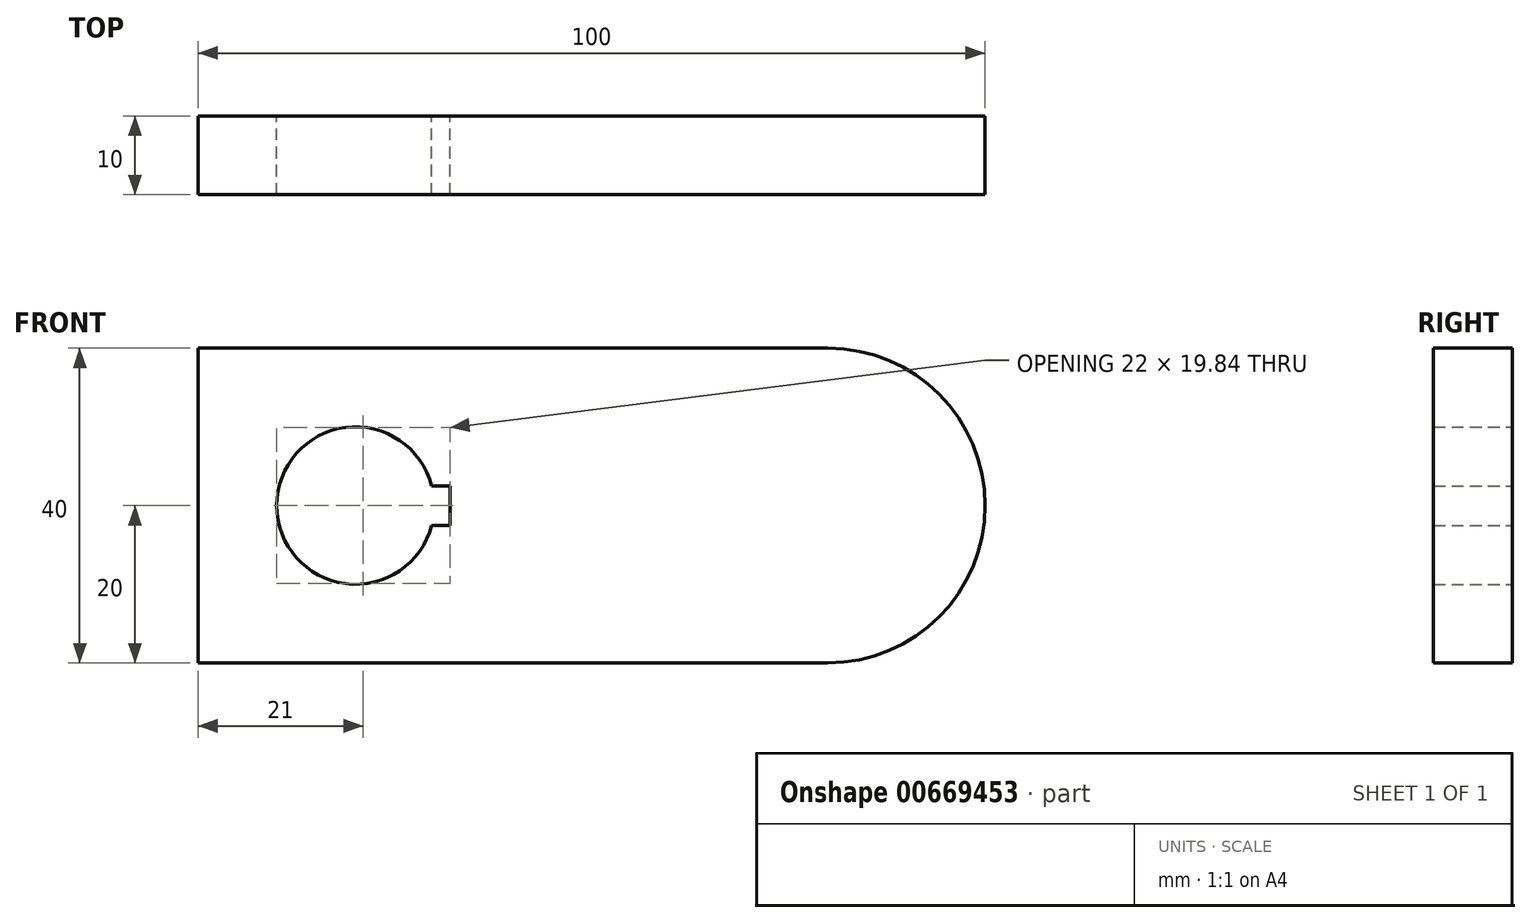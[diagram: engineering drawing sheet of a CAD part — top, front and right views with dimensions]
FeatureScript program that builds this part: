
annotation { "Feature Type Name" : "Feature", "Feature Type Description" : "" }
export const myFeature = defineFeature(function(context is Context, id is Id, definition is map)
    precondition{}
    {
        {
            var Q0;
            Q0=qCreatedBy(makeId("Front.planeOp"),FACE);
            var sketch = newSketch(context, id + "F0", { "sketchPlane" : qUnion([Q0])});
            skLineSegment(sketch, "E0.bottom", {"start": v(-80, 40) * mm, "end": v(0, 40) * mm});
            skLineSegment(sketch, "E0.top", {"start": v(-80, 0) * mm, "end": v(0, 0) * mm});
            skLineSegment(sketch, "E0.left", {"start": v(-80, 40) * mm, "end": v(-80, 0) * mm});
            skArc(sketch, "E1", {"start": v(-50.32, 22.5) * mm, "mid": v(-70, 20) * mm, "end": v(-50.32, 17.5) * mm});
            skPoint(sketch, "E2.centerSnap0", {"position": v(0, 20) * mm});
            skArc(sketch, "E3", {"start": v(0, 0) * mm, "mid": v(20, 20) * mm, "end": v(0, 40) * mm});
            skLineSegment(sketch, "E4", {"start": v(-60, 20) * mm, "end": v(-48, 20) * mm, "construction": true});
            skLineSegment(sketch, "E5", {"start": v(-48, 20) * mm, "end": v(-48, 22.5) * mm});
            skLineSegment(sketch, "E6", {"start": v(-48, 20) * mm, "end": v(-48, 17.5) * mm});
            skLineSegment(sketch, "E7", {"start": v(-48, 22.5) * mm, "end": v(-50.32, 22.5) * mm});
            skLineSegment(sketch, "E8", {"start": v(-48, 17.5) * mm, "end": v(-50.32, 17.5) * mm});
            skSolve(sketch);
        }
        {
            var Q0;
            Q0 = qSketchRegion(id + "F0", true);
            extrude(context, id + "F1", {"entities" : qUnion([Q0]), "depth" : 10 * mm, "offsetDistance" : 25 * mm});
        }
    });
